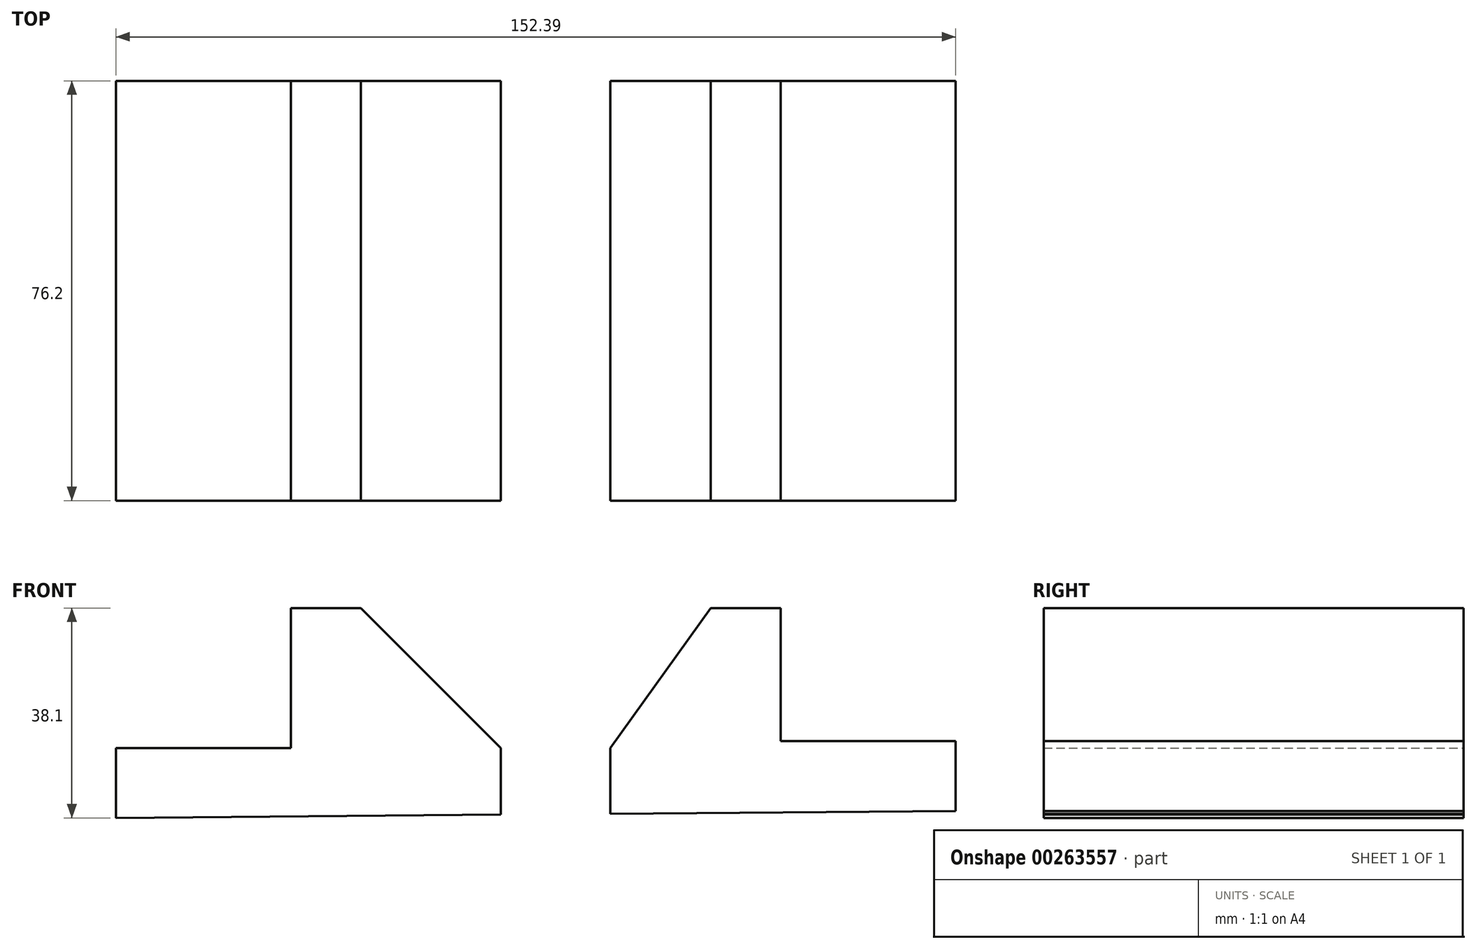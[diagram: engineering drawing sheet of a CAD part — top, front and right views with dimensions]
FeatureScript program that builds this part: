
annotation { "Feature Type Name" : "Feature", "Feature Type Description" : "" }
export const myFeature = defineFeature(function(context is Context, id is Id, definition is map)
    precondition{}
    {
        {
            var Q0;
            Q0=qCreatedBy(makeId("Front.planeOp"),FACE);
            var sketch = newSketch(context, id + "F0", { "sketchPlane" : qUnion([Q0])});
            skLineSegment(sketch, "E0", {"start": v(-69.85, -25.4) * mm, "end": v(-69.85, -12.7) * mm});
            skLineSegment(sketch, "E1", {"start": v(-69.85, -12.7) * mm, "end": v(-38.1, -12.7) * mm});
            skLineSegment(sketch, "E2", {"start": v(-38.1, -12.7) * mm, "end": v(-38.1, 12.7) * mm});
            skLineSegment(sketch, "E3", {"start": v(-38.1, 12.7) * mm, "end": v(-25.4, 12.7) * mm});
            skLineSegment(sketch, "E4", {"start": v(38.1, 12.7) * mm, "end": v(50.8, 12.7) * mm});
            skLineSegment(sketch, "E5", {"start": v(50.8, 12.7) * mm, "end": v(50.8, -11.43) * mm});
            skLineSegment(sketch, "E6", {"start": v(50.8, -11.43) * mm, "end": v(82.54, -11.43) * mm});
            skLineSegment(sketch, "E7", {"start": v(82.54, -11.43) * mm, "end": v(82.54, -24.13) * mm});
            skLineSegment(sketch, "E8", {"start": v(82.54, -24.13) * mm, "end": v(-69.85, -25.4) * mm});
            skLineSegment(sketch, "E9", {"start": v(-25.4, 12.7) * mm, "end": v(0, -12.7) * mm});
            skLineSegment(sketch, "E10", {"start": v(38.1, 12.7) * mm, "end": v(19.87, -12.7) * mm});
            skPoint(sketch, "E11.end.orphan", {"position": v(12.7, 0) * mm});
            skLineSegment(sketch, "E12", {"start": v(0, -12.7) * mm, "end": v(0, -24.82) * mm});
            skLineSegment(sketch, "E13", {"start": v(19.87, -12.7) * mm, "end": v(19.87, -24.65) * mm});
            skPoint(sketch, "E14.start.orphan", {"position": v(0, 0) * mm});
            skPoint(sketch, "E15.end.orphan", {"position": v(19.87, 0) * mm});
            skSolve(sketch);
        }
        {
            var Q0;
            Q0 = qSketchRegion(id + "F0", true);
            extrude(context, id + "F1", {"entities" : qUnion([Q0]), "depth" : 76.2 * mm});
        }
    });
